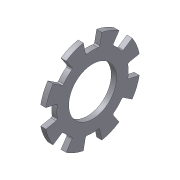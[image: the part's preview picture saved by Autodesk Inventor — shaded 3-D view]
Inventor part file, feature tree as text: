
AUTODESK INVENTOR PART (.ipt)
format: ipt  version: 2013 (Build 170138000, 138)  size: 130,560 bytes
history: native  units: mm (DEFAULTED — no unit token found)
features: sketch x2, extrude x1, pattern_circular x1
ambient origin geometry x8: Origin, YZ Plane, XZ Plane, XY Plane, X Axis, Y Axis, Z Axis, Center Point
bodies: Solid1 (feature_tree), Body (feature_tree)
feature tree (4):
  extrude  "Cut"  Depth=6.5024mm
  pattern_circular  "Cuts"  [2 undecoded]
  sketch  "Sketch1"  dims[d0=12.954mm d1=6.5024mm]
  sketch  "Sketch2"  dims[d2=0.7112mm d3=0.0mm d4=22.5deg d5=9.7282mm d6=0.7112mm d7=0.0mm d8=0.19431mm d9=80.0mm d11=360.0deg d12=0.0mm d13=0.0mm]
note: 2 required parameter values undecoded (feature->parameter linkage not recoverable at this tier; creation-order binding heuristic only, values carry confidence <= 0.55)
